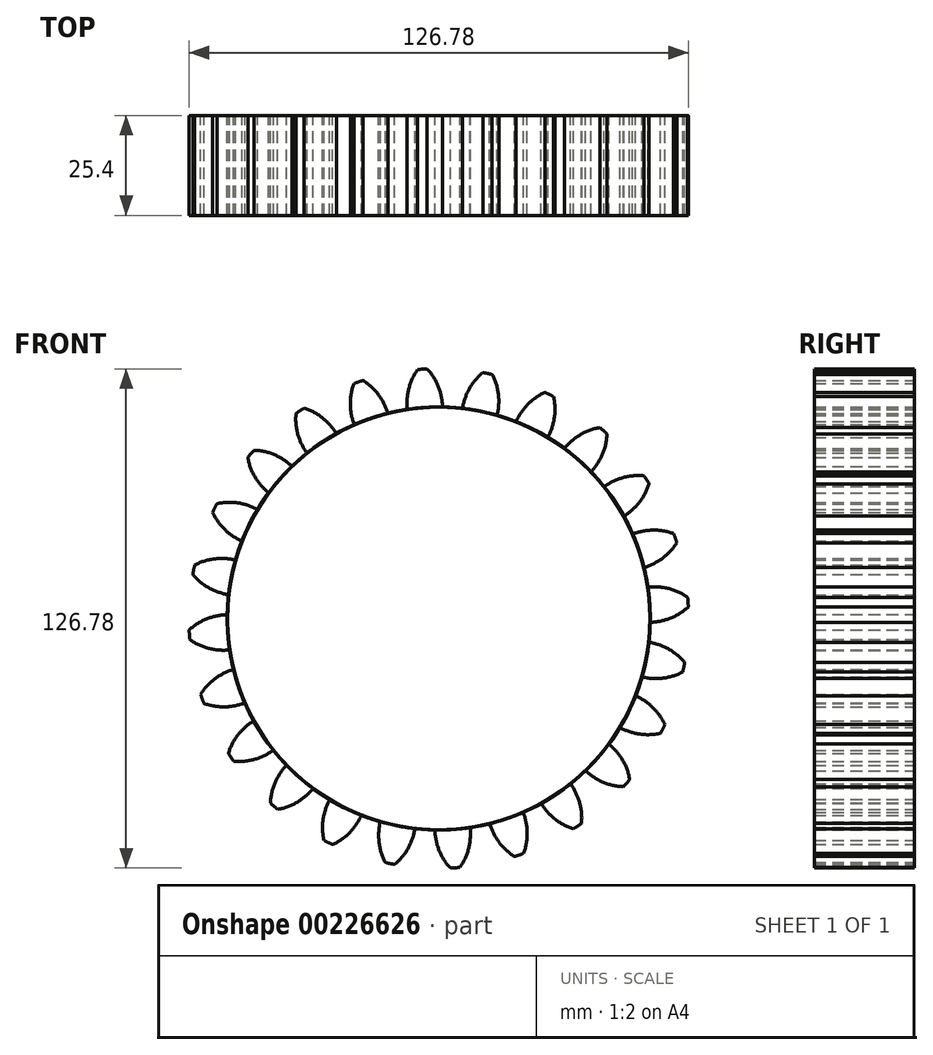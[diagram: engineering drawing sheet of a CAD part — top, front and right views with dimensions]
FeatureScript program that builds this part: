
annotation { "Feature Type Name" : "Feature", "Feature Type Description" : "" }
export const myFeature = defineFeature(function(context is Context, id is Id, definition is map)
    precondition{}
    {
        {
            var Q0;
            Q0=qCreatedBy(makeId("Front.planeOp"),FACE);
            var sketch = newSketch(context, id + "F0", { "sketchPlane" : qUnion([Q0])});
            skCircle(sketch, "E0", {"center": v(0, 0) * mm, "radius": 53.72 * mm});
            skCircle(sketch, "E1", {"center": v(0, 0) * mm, "radius": 58.67 * mm, "construction": true});
            skCircle(sketch, "E2", {"center": v(0, 0) * mm, "radius": 63.5 * mm, "construction": true});
            skLineSegment(sketch, "E3", {"start": v(0, 0) * mm, "end": v(0, 79.62) * mm, "construction": true});
            skLineSegment(sketch, "E4", {"start": v(0, 0) * mm, "end": v(-5.18, 79.03) * mm, "construction": true});
            skLineSegment(sketch, "E5", {"start": v(0, 58.67) * mm, "end": v(-87.59, 58.67) * mm, "construction": true});
            skLineSegment(sketch, "E6", {"start": v(0, 58.67) * mm, "end": v(-87.75, 26.74) * mm, "construction": true});
            skCircle(sketch, "E7", {"center": v(0, 58.67) * mm, "radius": 14.6 * mm, "construction": true});
            skCircle(sketch, "E8", {"center": v(0, 0) * mm, "radius": 55.14 * mm, "construction": true});
            skCircle(sketch, "E9", {"center": v(-13.62, 53.43) * mm, "radius": 14.6 * mm, "construction": true});
            skArc(sketch, "E10", {"start": v(0, 58.67) * mm, "mid": v(-1.23, 61.18) * mm, "end": v(-2.93, 63.39) * mm});
            skArc(sketch, "E11", {"start": v(0.98, 53.71) * mm, "mid": v(0.7, 56.23) * mm, "end": v(0, 58.67) * mm});
            skArc(sketch, "E12.MirrorCS", {"start": v(-7.66, 58.17) * mm, "mid": v(-6.76, 60.81) * mm, "end": v(-5.36, 63.23) * mm});
            skArc(sketch, "E13.MirrorCS", {"start": v(-7.99, 53.12) * mm, "mid": v(-8.03, 55.66) * mm, "end": v(-7.66, 58.17) * mm});
            skArc(sketch, "E14", {"start": v(-2.93, 63.39) * mm, "mid": v(-4.15, 63.34) * mm, "end": v(-5.36, 63.23) * mm});
            skSolve(sketch);
        }
        {
            var Q0;
            {var subQ0=sQuery(id+"F0.wireOp",EDGE,"E0");var subQ1=makeQuery(id+"F0.imprint","INTERSECT",VERTEX,{"derivedFrom":[subQ0,sQuery(id+"F0.wireOp",EDGE,"E11")]});Q0=makeQuery(id+"F0.imprint","IMPRINT",FACE,{"disambiguationData":[TD([[makeQuery(id+"F0.imprint","IMPRINT",EDGE,{"disambiguationData":[TD([[subQ1,-1.0]])],"derivedFrom":subQ0}),1.0]])]});}
            var Q1;
            Q1=makeQuery(id+"F0.imprint","IMPRINT",FACE,{"disambiguationData":[TD([[makeQuery(id+"F0.imprint","IMPRINT",EDGE,{"derivedFrom":sQuery(id+"F0.wireOp",EDGE,"E10")}),1.0]])]});
            extrude(context, id + "F1", {"entities" : qUnion([Q0, Q1]), "depth" : 25.4 * mm});
        }
        {
            var Q0;
            Q0=makeQuery(id+"F1.opExtrude","SWEPT_BODY",BODY,{"disambiguationData":[OSD([sQuery(id+"F0.wireOp",EDGE,"E0"),sQuery(id+"F0.wireOp",EDGE,"E10"),sQuery(id+"F0.wireOp",EDGE,"E11"),sQuery(id+"F0.wireOp",EDGE,"E12.MirrorCS"),sQuery(id+"F0.wireOp",EDGE,"E13.MirrorCS"),sQuery(id+"F0.wireOp",EDGE,"E14")])]});
            var Q1;
            Q1=makeQuery(id+"F1.opExtrude","SWEPT_FACE",FACE,{"disambiguationData":[OSD([sQuery(id+"F0.wireOp",EDGE,"E0")])]});
            circularPattern(context, id + "F2", {"entities" : qUnion([Q0]), "axis" : qUnion([Q1]), "angle" : 360 * degree, "instanceCount" : 24, "equalSpace" : true});
        }
    });
